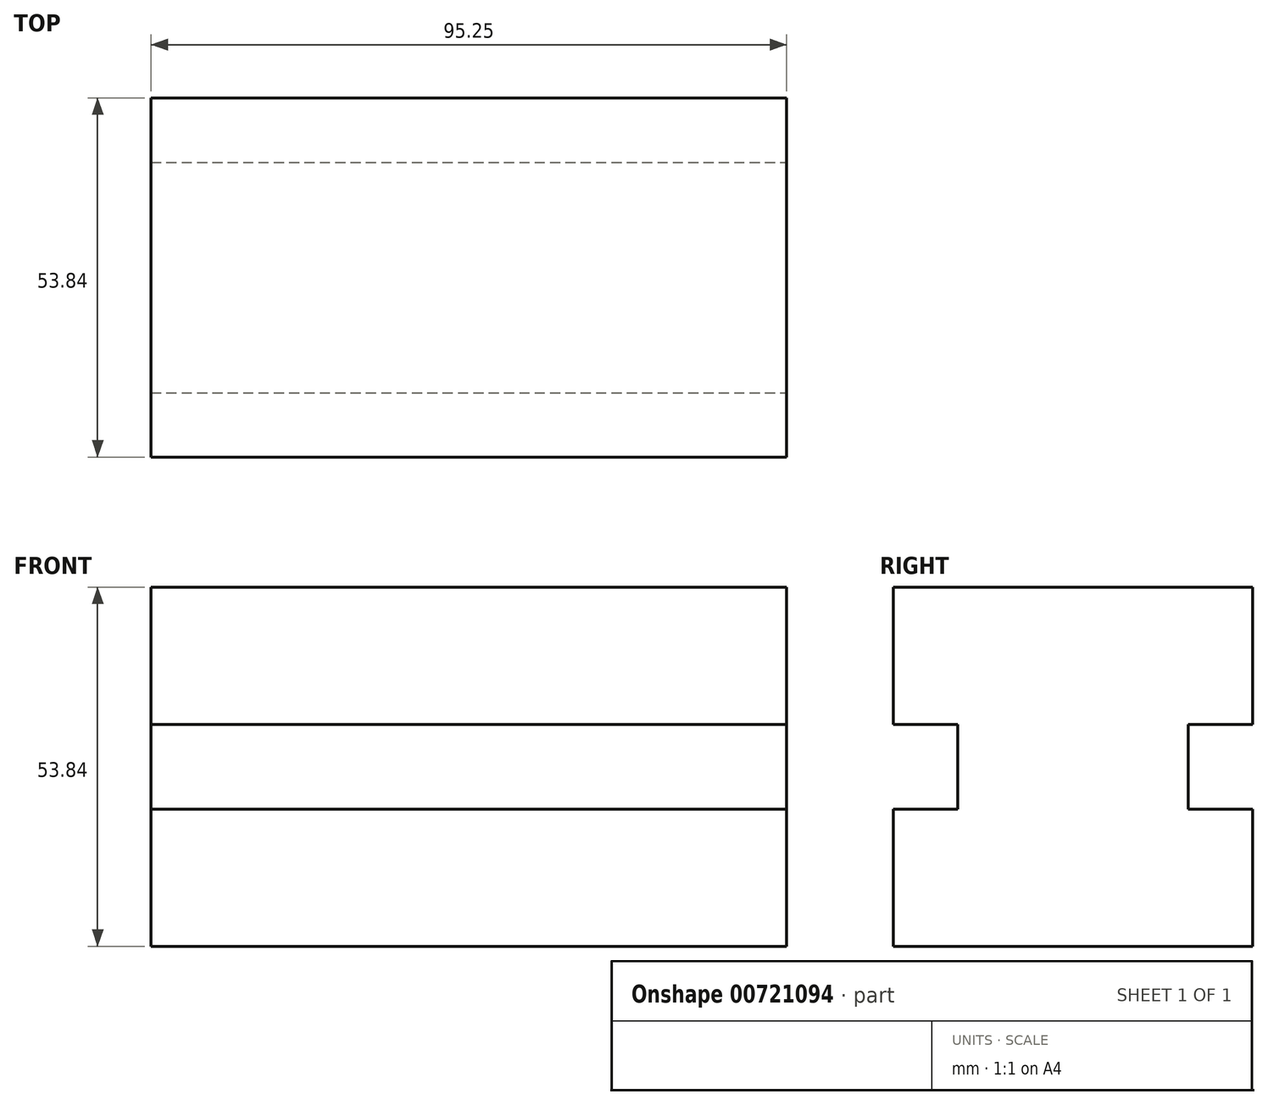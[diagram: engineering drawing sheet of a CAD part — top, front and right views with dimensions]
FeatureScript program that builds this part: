
annotation { "Feature Type Name" : "Feature", "Feature Type Description" : "" }
export const myFeature = defineFeature(function(context is Context, id is Id, definition is map)
    precondition{}
    {
        {
            var Q0;
            Q0=qCreatedBy(makeId("Right.planeOp"),FACE);
            var sketch = newSketch(context, id + "F0", { "sketchPlane" : qUnion([Q0])});
            skLineSegment(sketch, "E0.bottom", {"start": v(26.92, -26.92) * mm, "end": v(-26.92, -26.92) * mm});
            skLineSegment(sketch, "E0.top", {"start": v(26.92, 26.92) * mm, "end": v(-26.92, 26.92) * mm});
            skLineSegment(sketch, "E0.left", {"start": v(26.92, -26.92) * mm, "end": v(26.92, -6.35) * mm});
            skLineSegment(sketch, "E0.right", {"start": v(-26.92, -26.92) * mm, "end": v(-26.92, -6.35) * mm});
            skPoint(sketch, "E0.middle", {"position": v(0, 0) * mm});
            skLineSegment(sketch, "E1.bottom", {"start": v(-26.92, 6.35) * mm, "end": v(-17.27, 6.35) * mm});
            skLineSegment(sketch, "E1.top", {"start": v(-26.92, -6.35) * mm, "end": v(-17.27, -6.35) * mm});
            skLineSegment(sketch, "E1.right", {"start": v(-17.27, 6.35) * mm, "end": v(-17.27, -6.35) * mm});
            skLineSegment(sketch, "E2", {"start": v(0, 37.8) * mm, "end": v(0, -42.21) * mm, "construction": true});
            skPoint(sketch, "E2.startSnap0", {"position": v(0, 26.92) * mm});
            skLineSegment(sketch, "E3.MirrorCS", {"start": v(26.92, 6.35) * mm, "end": v(17.27, 6.35) * mm});
            skLineSegment(sketch, "E4.MirrorCS", {"start": v(17.27, 6.35) * mm, "end": v(17.27, -6.35) * mm});
            skLineSegment(sketch, "E5.MirrorCS", {"start": v(26.92, -6.35) * mm, "end": v(17.27, -6.35) * mm});
            skLineSegment(sketch, "E6.trimOffspring", {"start": v(-26.92, 6.35) * mm, "end": v(-26.92, 26.92) * mm});
            skLineSegment(sketch, "E7.trimOffspring", {"start": v(26.92, 6.35) * mm, "end": v(26.92, 26.92) * mm});
            skSolve(sketch);
        }
        {
            var Q0;
            Q0=makeQuery(id+"F0.imprint","IMPRINT",FACE,{"disambiguationData":[TD([[makeQuery(id+"F0.imprint","IMPRINT",EDGE,{"derivedFrom":sQuery(id+"F0.wireOp",EDGE,"E0.bottom")}),-1.0]])]});
            extrude(context, id + "F1", {"entities" : qUnion([Q0]), "oppositeDirection" : true, "depth" : 95.25 * mm, "offsetDistance" : 25.4 * mm});
        }
    });
